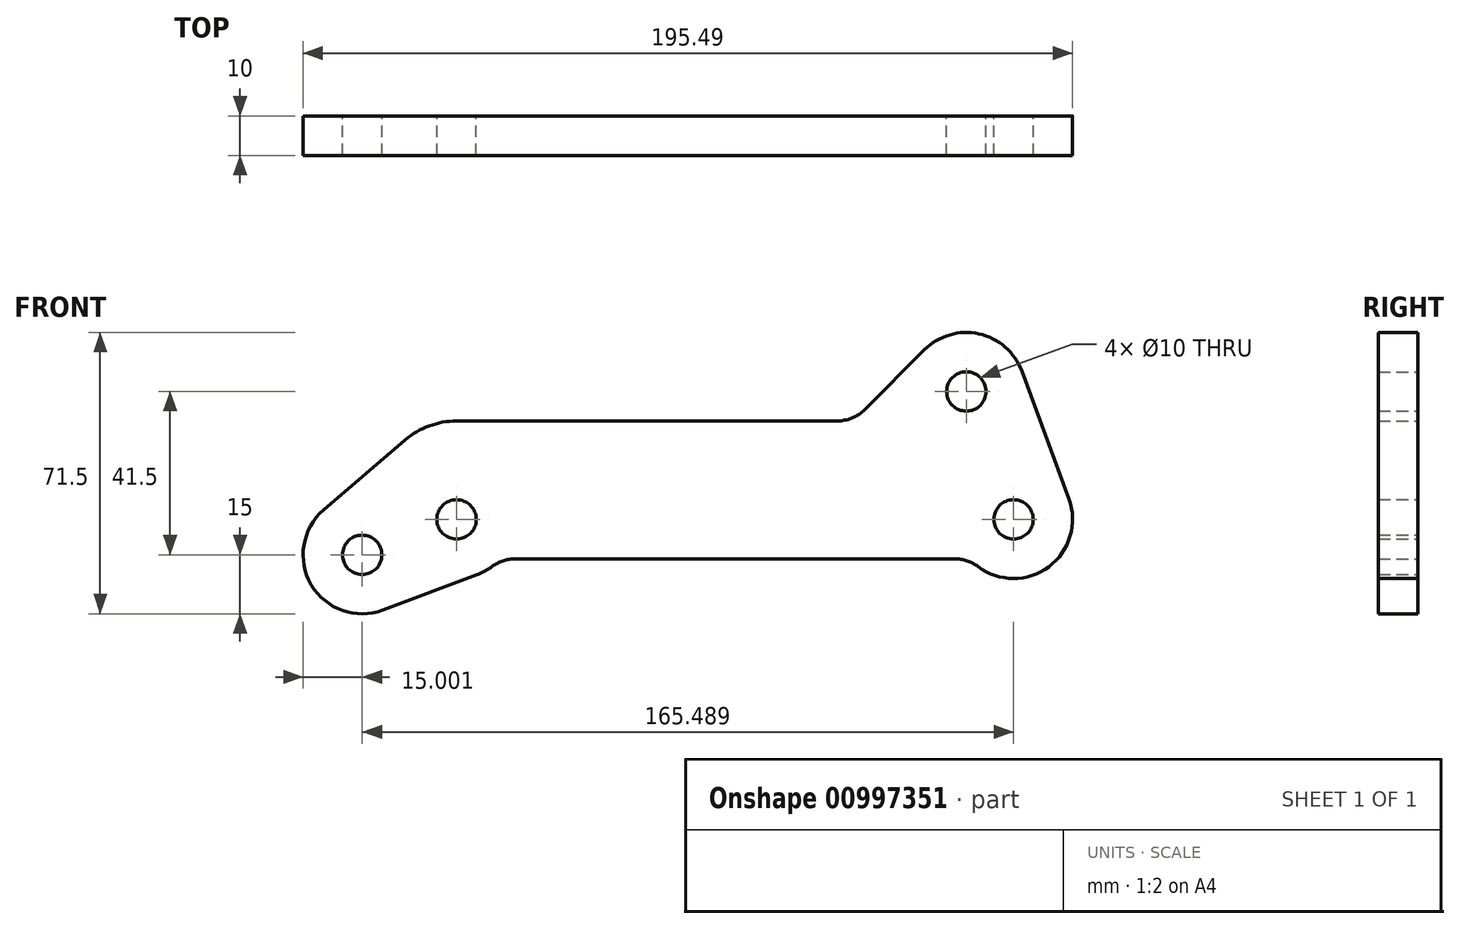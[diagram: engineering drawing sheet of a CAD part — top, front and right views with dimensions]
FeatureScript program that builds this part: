
annotation { "Feature Type Name" : "Feature", "Feature Type Description" : "" }
export const myFeature = defineFeature(function(context is Context, id is Id, definition is map)
    precondition{}
    {
        {
            var Q0;
            Q0=qCreatedBy(makeId("Front.planeOp"),FACE);
            var sketch = newSketch(context, id + "F0", { "sketchPlane" : qUnion([Q0])});
            skCircle(sketch, "E0", {"center": v(-71.5, 0) * mm, "radius": 5 * mm});
            skCircle(sketch, "E1", {"center": v(70, 0) * mm, "radius": 5 * mm});
            skArc(sketch, "E2.0", {"start": v(-66.23, -14.04) * mm, "mid": v(-64.3, -13.15) * mm, "end": v(-62.5, -12) * mm});
            skArc(sketch, "E3.0", {"start": v(61, -12) * mm, "mid": v(78.96, -12.03) * mm, "end": v(84.07, 5.2) * mm});
            skCircle(sketch, "E4", {"center": v(58, 32.5) * mm, "radius": 5 * mm});
            skCircle(sketch, "E5", {"center": v(-95.49, -9) * mm, "radius": 5 * mm});
            skArc(sketch, "E6.0", {"start": v(-105.26, 2.38) * mm, "mid": v(-108.4, -16.64) * mm, "end": v(-90.22, -23.04) * mm});
            skArc(sketch, "E7.0", {"start": v(72.07, 37.7) * mm, "mid": v(61.21, 47.15) * mm, "end": v(47.4, 43.1) * mm});
            skLineSegment(sketch, "E8", {"start": v(-56.5, -10) * mm, "end": v(55, -10) * mm});
            skLineSegment(sketch, "E9", {"start": v(32.22, 27.93) * mm, "end": v(47.4, 43.1) * mm});
            skLineSegment(sketch, "E10", {"start": v(-90.22, -23.04) * mm, "end": v(-66.23, -14.04) * mm});
            skLineSegment(sketch, "E11", {"start": v(84.07, 5.2) * mm, "end": v(72.07, 37.7) * mm});
            skPoint(sketch, "E12.visualSharp", {"position": v(-60.32, -10) * mm});
            skArc(sketch, "E12.filletArc", {"start": v(-56.5, -10) * mm, "mid": v(-59.66, -10.51) * mm, "end": v(-62.5, -12) * mm});
            skPoint(sketch, "E13.visualSharp", {"position": v(58.82, -10) * mm});
            skArc(sketch, "E13.filletArc", {"start": v(61, -12) * mm, "mid": v(58.16, -10.51) * mm, "end": v(55, -10) * mm});
            skLineSegment(sketch, "E14", {"start": v(25.14, 25) * mm, "end": v(-71.5, 25) * mm});
            skLineSegment(sketch, "E15", {"start": v(-105.26, 2.38) * mm, "end": v(-84.53, 20.18) * mm});
            skArc(sketch, "E16.trimOffspring", {"start": v(-71.5, 25) * mm, "mid": v(-78.45, 23.76) * mm, "end": v(-84.53, 20.18) * mm});
            skPoint(sketch, "E17.visualSharp", {"position": v(29.29, 25) * mm});
            skArc(sketch, "E17.filletArc", {"start": v(25.14, 25) * mm, "mid": v(28.97, 25.76) * mm, "end": v(32.22, 27.93) * mm});
            skSolve(sketch);
        }
        {
            var Q0;
            Q0 = qSketchRegion(id + "F0", true);
            extrude(context, id + "F1", {"entities" : qUnion([Q0]), "depth" : 10 * mm, "offsetDistance" : 25 * mm});
        }
    });
